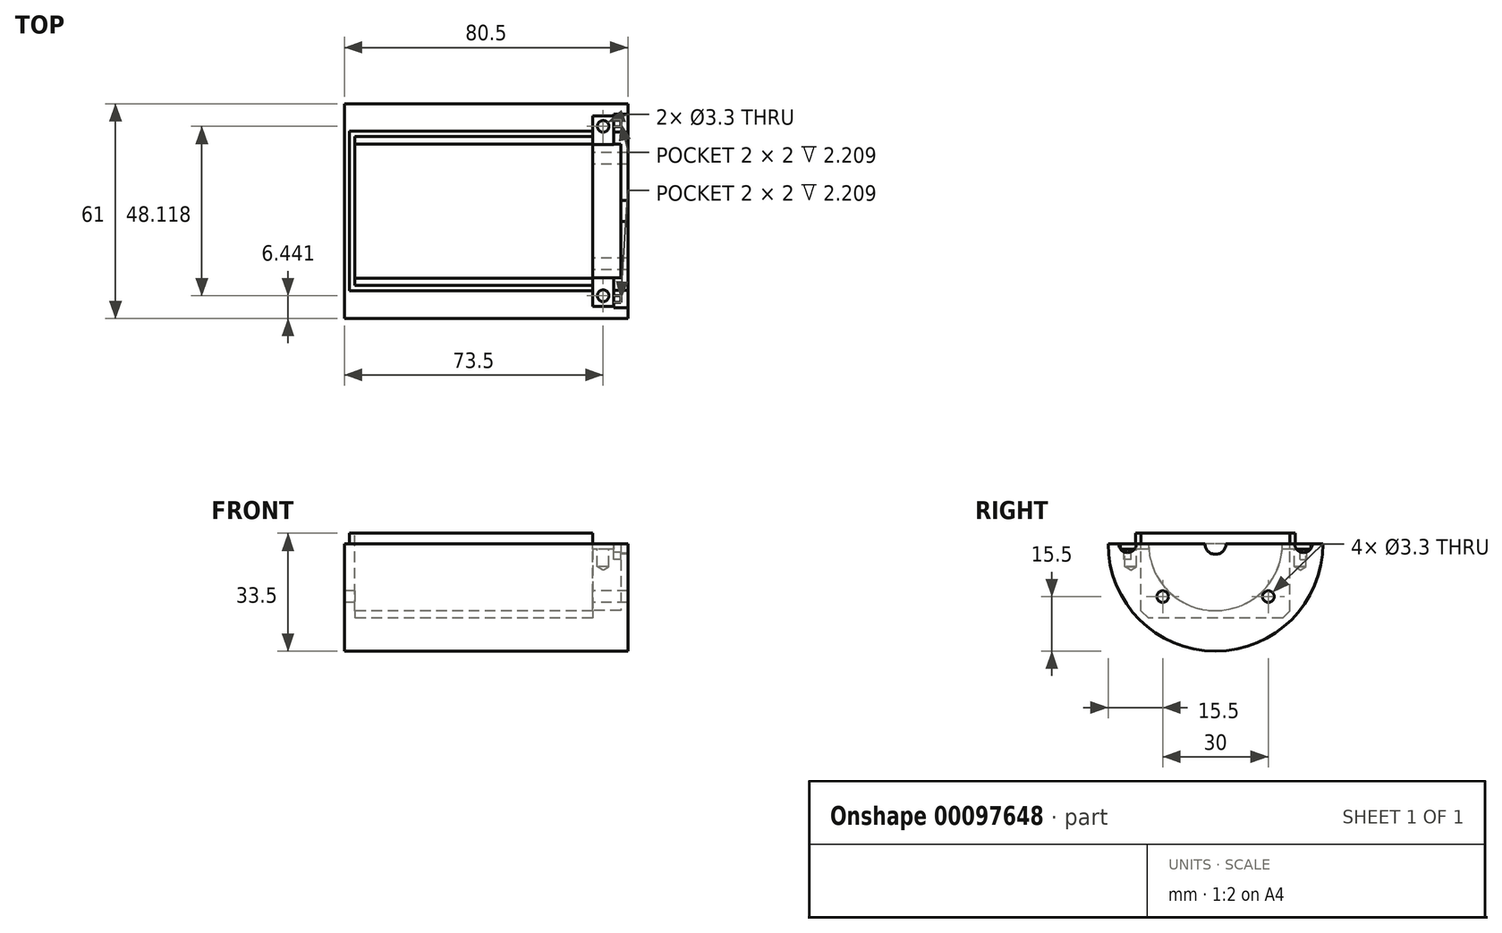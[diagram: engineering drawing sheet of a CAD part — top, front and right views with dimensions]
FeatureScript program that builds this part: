
annotation { "Feature Type Name" : "Feature", "Feature Type Description" : "" }
export const myFeature = defineFeature(function(context is Context, id is Id, definition is map)
    precondition{}
    {
        {
            var Q0;
            Q0=qCreatedBy(makeId("Right.planeOp"),FACE);
            var sketch = newSketch(context, id + "F0", { "sketchPlane" : qUnion([Q0])});
            skArc(sketch, "E0", {"start": v(-30.5, 0) * mm, "mid": v(0, -30.5) * mm, "end": v(30.5, 0) * mm});
            skLineSegment(sketch, "E1.bottom", {"start": v(19.03, -21.15) * mm, "end": v(-19.03, -21.15) * mm});
            skLineSegment(sketch, "E1.left", {"start": v(21.15, -19.03) * mm, "end": v(21.15, 0) * mm});
            skLineSegment(sketch, "E1.right", {"start": v(-21.15, -19.03) * mm, "end": v(-21.15, 0) * mm});
            skLineSegment(sketch, "E2", {"start": v(-30.5, 0) * mm, "end": v(30.5, 0) * mm});
            skPoint(sketch, "E2.endSnap0", {"position": v(21.15, 0) * mm});
            skLineSegment(sketch, "E3", {"start": v(-21.15, -19.03) * mm, "end": v(-19.03, -21.15) * mm});
            skLineSegment(sketch, "E4.MirrorCS", {"start": v(21.15, -19.03) * mm, "end": v(19.03, -21.15) * mm});
            skSolve(sketch);
        }
        {
            var Q0;
            {var subQ0=sQuery(id+"F0.wireOp",EDGE,"E2");var subQ3=sQuery(id+"F0.wireOp",EDGE,"E1.right");var subQ6=makeQuery(id+"F0.imprint","INTERSECT",VERTEX,{"derivedFrom":[subQ3,subQ0]});Q0=makeQuery(id+"F0.imprint","IMPRINT",FACE,{"disambiguationData":[TD([[makeQuery(id+"F0.imprint","IMPRINT",EDGE,{"disambiguationData":[TD([[subQ6,1.0]])],"derivedFrom":subQ3}),1.0]])]});}
            var Q1;
            {var subQ0=sQuery(id+"F0.wireOp",EDGE,"E1.bottom");var subQ5=makeQuery(id+"F0.imprint","INTERSECT",VERTEX,{"derivedFrom":[subQ0,sQuery(id+"F0.wireOp",EDGE,"E3")]});Q1=makeQuery(id+"F0.imprint","IMPRINT",FACE,{"disambiguationData":[TD([[makeQuery(id+"F0.imprint","IMPRINT",EDGE,{"disambiguationData":[TD([[subQ5,1.0]])],"derivedFrom":subQ0}),1.0]])]});}
            var Q2;
            {var subQ0=sQuery(id+"F0.wireOp",EDGE,"E2");var subQ3=sQuery(id+"F0.wireOp",EDGE,"E1.left");var subQ6=makeQuery(id+"F0.imprint","INTERSECT",VERTEX,{"derivedFrom":[subQ3,subQ0]});Q2=makeQuery(id+"F0.imprint","IMPRINT",FACE,{"disambiguationData":[TD([[makeQuery(id+"F0.imprint","IMPRINT",EDGE,{"disambiguationData":[TD([[subQ6,1.0]])],"derivedFrom":subQ3}),-1.0]])]});}
            var Q3;
            {var subQ3=sQuery(id+"F0.wireOp",EDGE,"E4.MirrorCS");Q3=makeQuery(id+"F0.imprint","IMPRINT",FACE,{"disambiguationData":[TD([[makeQuery(id+"F0.imprint","IMPRINT",EDGE,{"derivedFrom":subQ3}),1.0]])]});}
            var Q4;
            {var subQ3=sQuery(id+"F0.wireOp",EDGE,"E3");Q4=makeQuery(id+"F0.imprint","IMPRINT",FACE,{"disambiguationData":[TD([[makeQuery(id+"F0.imprint","IMPRINT",EDGE,{"derivedFrom":subQ3}),-1.0]])]});}
            extrude(context, id + "F1", {"entities" : qUnion([Q0, Q1, Q2, Q3, Q4]), "endBound" : BoundingType.SYMMETRIC, "depth" : 67.5 * mm});
        }
        {
            var Q0;
            Q0=makeQuery(id+"F1.opExtrude","CAP_FACE",FACE,{"disambiguationData":[OSD([sQuery(id+"F0.wireOp",EDGE,"E0"),sQuery(id+"F0.wireOp",EDGE,"E1.bottom"),sQuery(id+"F0.wireOp",EDGE,"E1.left"),sQuery(id+"F0.wireOp",EDGE,"E1.right"),sQuery(id+"F0.wireOp",EDGE,"E2"),sQuery(id+"F0.wireOp",EDGE,"E3"),sQuery(id+"F0.wireOp",EDGE,"E4.MirrorCS")])],"isStart":false});
            var sketch = newSketch(context, id + "F2", { "sketchPlane" : qUnion([Q0])});
            skArc(sketch, "E5", {"start": v(-30.5, 0) * mm, "mid": v(0, -30.5) * mm, "end": v(30.5, 0) * mm});
            skLineSegment(sketch, "E6", {"start": v(-30.5, 0) * mm, "end": v(30.5, 0) * mm});
            skSolve(sketch);
        }
        {
            var Q0;
            Q0=makeQuery(id+"F2.imprint","IMPRINT",FACE,{"disambiguationData":[TD([[makeQuery(id+"F2.imprint","IMPRINT",EDGE,{"derivedFrom":makeQuery(id+"F1.opExtrude","CAP_EDGE",EDGE,{"disambiguationData":[OSD([sQuery(id+"F0.wireOp",EDGE,"E1.bottom")])],"isStart":false})}),-1.0]])]});
            var Q1;
            {var subQ1=sQuery(id+"F2.wireOp",EDGE,"E5");Q1=makeQuery(id+"F2.imprint","IMPRINT",FACE,{"disambiguationData":[TD([[makeQuery(id+"F2.imprint","IMPRINT",EDGE,{"derivedFrom":subQ1}),1.0]])]});}
            extrude(context, id + "F3", {"entities" : qUnion([Q0, Q1]), "operationType" : NewBodyOperationType.ADD, "depth" : 10 * mm});
        }
        {
            var Q0;
            Q0=makeQuery(id+"F1.opExtrude","CAP_FACE",FACE,{"disambiguationData":[OSD([sQuery(id+"F0.wireOp",EDGE,"E0"),sQuery(id+"F0.wireOp",EDGE,"E1.bottom"),sQuery(id+"F0.wireOp",EDGE,"E1.left"),sQuery(id+"F0.wireOp",EDGE,"E1.right"),sQuery(id+"F0.wireOp",EDGE,"E2"),sQuery(id+"F0.wireOp",EDGE,"E3"),sQuery(id+"F0.wireOp",EDGE,"E4.MirrorCS")])],"isStart":true});
            var sketch = newSketch(context, id + "F4", { "sketchPlane" : qUnion([Q0])});
            skArc(sketch, "E7", {"start": v(-30.5, 0) * mm, "mid": v(0, -30.5) * mm, "end": v(30.5, 0) * mm});
            skLineSegment(sketch, "E8", {"start": v(-30.5, 0) * mm, "end": v(30.5, 0) * mm});
            skSolve(sketch);
        }
        {
            var Q0;
            Q0=makeQuery(id+"F4.imprint","IMPRINT",FACE,{"disambiguationData":[TD([[makeQuery(id+"F4.imprint","IMPRINT",EDGE,{"derivedFrom":makeQuery(id+"F1.opExtrude","CAP_EDGE",EDGE,{"disambiguationData":[OSD([sQuery(id+"F0.wireOp",EDGE,"E1.bottom")])],"isStart":true})}),1.0]])]});
            var Q1;
            {var subQ1=sQuery(id+"F4.wireOp",EDGE,"E7");Q1=makeQuery(id+"F4.imprint","IMPRINT",FACE,{"disambiguationData":[TD([[makeQuery(id+"F4.imprint","IMPRINT",EDGE,{"derivedFrom":subQ1}),-1.0]])]});}
            extrude(context, id + "F5", {"entities" : qUnion([Q0, Q1]), "operationType" : NewBodyOperationType.ADD, "depth" : 3 * mm});
        }
        {
            var Q0;
            {var subQ0=sQuery(id+"F0.wireOp",EDGE,"E2");var subQ1=sQuery(id+"F0.wireOp",EDGE,"E0");Q0=makeQuery(id+"F5.boolean.opBoolean","MERGE",FACE,{"derivedFrom":[makeQuery(id+"F3.boolean.opBoolean","MERGE",FACE,{"derivedFrom":[makeQuery(id+"F1.opExtrude","SWEPT_FACE",FACE,{"disambiguationData":[OSD([subQ0]),TDD([makeQuery(id+"F0.imprint","IMPRINT",EDGE,{"disambiguationData":[TD([[makeQuery(id+"F0.imprint","INTERSECT",VERTEX,{"disambiguationData":[OD(0.0)],"derivedFrom":[subQ1,subQ0]}),-1.0]])],"derivedFrom":subQ0})])]}),makeQuery(id+"F1.opExtrude","SWEPT_FACE",FACE,{"disambiguationData":[OSD([subQ0]),TDD([makeQuery(id+"F0.imprint","IMPRINT",EDGE,{"disambiguationData":[TD([[makeQuery(id+"F0.imprint","INTERSECT",VERTEX,{"disambiguationData":[OD(1.0)],"derivedFrom":[subQ1,subQ0]}),1.0]])],"derivedFrom":subQ0})])]}),makeQuery(id+"F3.opExtrude","SWEPT_FACE",FACE,{"disambiguationData":[OSD([sQuery(id+"F2.wireOp",EDGE,"E6")])]})]}),makeQuery(id+"F5.opExtrude","SWEPT_FACE",FACE,{"disambiguationData":[OSD([sQuery(id+"F4.wireOp",EDGE,"E8")])]})]});}
            var sketch = newSketch(context, id + "F6", { "sketchPlane" : qUnion([Q0])});
            skLineSegment(sketch, "E9.bottom", {"start": v(33.75, 0) * mm, "end": v(41.75, 0) * mm});
            skLineSegment(sketch, "E9.top", {"start": v(33.75, 19) * mm, "end": v(41.75, 19) * mm});
            skLineSegment(sketch, "E9.left", {"start": v(33.75, 0) * mm, "end": v(33.75, 19) * mm});
            skLineSegment(sketch, "E9.right", {"start": v(41.75, 0) * mm, "end": v(41.75, 19) * mm});
            skLineSegment(sketch, "E10.bottom", {"start": v(43.75, 0) * mm, "end": v(41.75, 0) * mm});
            skLineSegment(sketch, "E10.top", {"start": v(43.75, 3) * mm, "end": v(41.75, 3) * mm});
            skLineSegment(sketch, "E10.left", {"start": v(43.75, 0) * mm, "end": v(43.75, 3) * mm});
            skLineSegment(sketch, "E10.right", {"start": v(41.75, 0) * mm, "end": v(41.75, 3) * mm});
            skLineSegment(sketch, "E11.bottom", {"start": v(39.75, -22.5) * mm, "end": v(43.75, -22.5) * mm});
            skLineSegment(sketch, "E11.top", {"start": v(39.75, -27.5) * mm, "end": v(43.75, -27.5) * mm});
            skLineSegment(sketch, "E11.left", {"start": v(39.75, -22.5) * mm, "end": v(39.75, -27.5) * mm});
            skLineSegment(sketch, "E11.right", {"start": v(43.75, -22.5) * mm, "end": v(43.75, -27.5) * mm});
            skLineSegment(sketch, "E12.MirrorCS", {"start": v(39.75, 22.5) * mm, "end": v(39.75, 27.5) * mm});
            skLineSegment(sketch, "E13.MirrorCS", {"start": v(39.75, 22.5) * mm, "end": v(43.75, 22.5) * mm});
            skLineSegment(sketch, "E14.MirrorCS", {"start": v(39.75, 27.5) * mm, "end": v(43.75, 27.5) * mm});
            skLineSegment(sketch, "E15.MirrorCS", {"start": v(43.75, 22.5) * mm, "end": v(43.75, 27.5) * mm});
            skLineSegment(sketch, "E16", {"start": v(39.75, -25) * mm, "end": v(43.75, -25) * mm});
            skLineSegment(sketch, "E17.MirrorCS", {"start": v(39.75, 25) * mm, "end": v(43.75, 25) * mm});
            skSolve(sketch);
        }
        {
            var Q0;
            Q0=makeQuery(id+"F6.imprint","IMPRINT",FACE,{"disambiguationData":[TD([[makeQuery(id+"F6.imprint","IMPRINT",EDGE,{"derivedFrom":sQuery(id+"F6.wireOp",EDGE,"E9.bottom")}),1.0]])]});
            var Q1;
            Q1=makeQuery(id+"F6.imprint","IMPRINT",FACE,{"disambiguationData":[TD([[makeQuery(id+"F6.imprint","IMPRINT",EDGE,{"derivedFrom":sQuery(id+"F6.wireOp",EDGE,"E10.bottom")}),-1.0]])]});
            var Q2;
            Q2=sQuery(id+"F6.wireOp",EDGE,"E9.bottom");
            revolve(context, id + "F7", {"operationType" : NewBodyOperationType.REMOVE, "entities" : qUnion([Q0, Q1]), "axis" : qUnion([Q2]), "revolveType" : RevolveType.FULL});
        }
        {
            var Q0;
            {var subQ0=sQuery(id+"F6.wireOp",EDGE,"E11.top");Q0=makeQuery(id+"F6.imprint","IMPRINT",FACE,{"disambiguationData":[TD([[makeQuery(id+"F6.imprint","IMPRINT",EDGE,{"derivedFrom":subQ0}),1.0]])]});}
            var Q1;
            Q1=sQuery(id+"F6.wireOp",EDGE,"E16");
            revolve(context, id + "F8", {"operationType" : NewBodyOperationType.REMOVE, "entities" : qUnion([Q0]), "axis" : qUnion([Q1]), "revolveType" : RevolveType.FULL, "oppositeDirection" : true});
        }
        {
            var Q0;
            {var subQ0=sQuery(id+"F6.wireOp",EDGE,"E13.MirrorCS");Q0=makeQuery(id+"F6.imprint","IMPRINT",FACE,{"disambiguationData":[TD([[makeQuery(id+"F6.imprint","IMPRINT",EDGE,{"derivedFrom":subQ0}),1.0]])]});}
            var Q1;
            Q1=sQuery(id+"F6.wireOp",EDGE,"E17.MirrorCS");
            revolve(context, id + "F9", {"operationType" : NewBodyOperationType.REMOVE, "entities" : qUnion([Q0]), "axis" : qUnion([Q1]), "revolveType" : RevolveType.FULL, "oppositeDirection" : true});
        }
        {
            var Q0;
            {var subQ16=sQuery(id+"F6.wireOp",EDGE,"E9.bottom");Q0=makeQuery(id+"F6.imprint","IMPRINT",FACE,{"disambiguationData":[TD([[makeQuery(id+"F6.imprint","IMPRINT",EDGE,{"derivedFrom":subQ16}),-1.0]])]});}
            var sketch = newSketch(context, id + "F10", { "sketchPlane" : qUnion([Q0])});
            skLineSegment(sketch, "E18.bottom", {"start": v(41.75, -26) * mm, "end": v(39.75, -26) * mm});
            skLineSegment(sketch, "E18.top", {"start": v(41.75, -24) * mm, "end": v(39.75, -24) * mm});
            skLineSegment(sketch, "E18.left", {"start": v(41.75, -26) * mm, "end": v(41.75, -24) * mm});
            skPoint(sketch, "E18.middle", {"position": v(39.75, -25) * mm});
            skLineSegment(sketch, "E19", {"start": v(39.75, -24) * mm, "end": v(39.75, -26) * mm});
            skPoint(sketch, "E18.right.end.orphan", {"position": v(37.75, -24) * mm});
            skPoint(sketch, "E20.orphan", {"position": v(37.75, -26) * mm});
            skLineSegment(sketch, "E21.MirrorCS", {"start": v(41.75, 24) * mm, "end": v(39.75, 24) * mm});
            skLineSegment(sketch, "E22.MirrorCS", {"start": v(41.75, 26) * mm, "end": v(41.75, 24) * mm});
            skLineSegment(sketch, "E23.MirrorCS", {"start": v(41.75, 26) * mm, "end": v(39.75, 26) * mm});
            skLineSegment(sketch, "E24.MirrorCS", {"start": v(39.75, 24) * mm, "end": v(39.75, 26) * mm});
            skSolve(sketch);
        }
        {
            var Q0;
            {var subQ5=sQuery(id+"F10.wireOp",EDGE,"E18.bottom");Q0=makeQuery(id+"F10.imprint","IMPRINT",FACE,{"disambiguationData":[TD([[makeQuery(id+"F10.imprint","IMPRINT",EDGE,{"derivedFrom":subQ5}),-1.0]])]});}
            var Q1;
            {var subQ2=sQuery(id+"F10.wireOp",EDGE,"E21.MirrorCS");Q1=makeQuery(id+"F10.imprint","IMPRINT",FACE,{"disambiguationData":[TD([[makeQuery(id+"F10.imprint","IMPRINT",EDGE,{"derivedFrom":subQ2}),-1.0]])]});}
            extrude(context, id + "F11", {"entities" : qUnion([Q0, Q1]), "operationType" : NewBodyOperationType.REMOVE, "oppositeDirection" : true, "depth" : 4.5 * mm});
        }
        {
            var Q0;
            {var subQ0=sQuery(id+"F0.wireOp",EDGE,"E2");var subQ1=sQuery(id+"F0.wireOp",EDGE,"E0");Q0=makeQuery(id+"F5.boolean.opBoolean","MERGE",FACE,{"derivedFrom":[makeQuery(id+"F3.boolean.opBoolean","MERGE",FACE,{"derivedFrom":[makeQuery(id+"F1.opExtrude","SWEPT_FACE",FACE,{"disambiguationData":[OSD([subQ0]),TDD([makeQuery(id+"F0.imprint","IMPRINT",EDGE,{"disambiguationData":[TD([[makeQuery(id+"F0.imprint","INTERSECT",VERTEX,{"disambiguationData":[OD(0.0)],"derivedFrom":[subQ1,subQ0]}),-1.0]])],"derivedFrom":subQ0})])]}),makeQuery(id+"F1.opExtrude","SWEPT_FACE",FACE,{"disambiguationData":[OSD([subQ0]),TDD([makeQuery(id+"F0.imprint","IMPRINT",EDGE,{"disambiguationData":[TD([[makeQuery(id+"F0.imprint","INTERSECT",VERTEX,{"disambiguationData":[OD(1.0)],"derivedFrom":[subQ1,subQ0]}),1.0]])],"derivedFrom":subQ0})])]}),makeQuery(id+"F3.opExtrude","SWEPT_FACE",FACE,{"disambiguationData":[OSD([sQuery(id+"F2.wireOp",EDGE,"E6")])]})]}),makeQuery(id+"F5.opExtrude","SWEPT_FACE",FACE,{"disambiguationData":[OSD([sQuery(id+"F4.wireOp",EDGE,"E8")])]})]});}
            var sketch = newSketch(context, id + "F12", { "sketchPlane" : qUnion([Q0])});
            skLineSegment(sketch, "E25.bottom", {"start": v(33.75, 27.06) * mm, "end": v(39.75, 27.06) * mm});
            skLineSegment(sketch, "E25.top", {"start": v(33.75, -27.06) * mm, "end": v(39.75, -27.06) * mm});
            skLineSegment(sketch, "E25.left", {"start": v(33.75, 27.06) * mm, "end": v(33.75, -27.06) * mm});
            skLineSegment(sketch, "E25.right", {"start": v(39.75, 27.06) * mm, "end": v(39.75, -27.06) * mm});
            skPoint(sketch, "E26", {"position": v(36.75, 24.06) * mm});
            skPoint(sketch, "E27.MirrorP", {"position": v(36.75, -24.06) * mm});
            skSolve(sketch);
        }
        {
            var Q0;
            {var subQ7=sQuery(id+"F12.wireOp",EDGE,"E25.bottom");Q0=makeQuery(id+"F12.imprint","IMPRINT",FACE,{"disambiguationData":[TD([[makeQuery(id+"F12.imprint","IMPRINT",EDGE,{"derivedFrom":subQ7}),-1.0]])]});}
            var Q1;
            {var subQ4=sQuery(id+"F12.wireOp",EDGE,"E25.top");Q1=makeQuery(id+"F12.imprint","IMPRINT",FACE,{"disambiguationData":[TD([[makeQuery(id+"F12.imprint","IMPRINT",EDGE,{"derivedFrom":subQ4}),1.0]])]});}
            var Q2;
            {var subQ0=sQuery(id+"F12.wireOp",EDGE,"E25.left");var subQ1=makeQuery(id+"F7.opRevolve","SWEPT_FACE",FACE,{"disambiguationData":[OSD([sQuery(id+"F6.wireOp",EDGE,"E9.top")])]});var subQ2=sQuery(id+"F0.wireOp",EDGE,"E2");var subQ3=sQuery(id+"F0.wireOp",EDGE,"E0");var subQ4=makeQuery(id+"F5.boolean.opBoolean","MERGE",FACE,{"derivedFrom":[makeQuery(id+"F3.boolean.opBoolean","MERGE",FACE,{"derivedFrom":[makeQuery(id+"F1.opExtrude","SWEPT_FACE",FACE,{"disambiguationData":[OSD([subQ2]),TDD([makeQuery(id+"F0.imprint","IMPRINT",EDGE,{"disambiguationData":[TD([[makeQuery(id+"F0.imprint","INTERSECT",VERTEX,{"disambiguationData":[OD(0.0)],"derivedFrom":[subQ3,subQ2]}),-1.0]])],"derivedFrom":subQ2})])]}),makeQuery(id+"F1.opExtrude","SWEPT_FACE",FACE,{"disambiguationData":[OSD([subQ2]),TDD([makeQuery(id+"F0.imprint","IMPRINT",EDGE,{"disambiguationData":[TD([[makeQuery(id+"F0.imprint","INTERSECT",VERTEX,{"disambiguationData":[OD(1.0)],"derivedFrom":[subQ3,subQ2]}),1.0]])],"derivedFrom":subQ2})])]}),makeQuery(id+"F3.opExtrude","SWEPT_FACE",FACE,{"disambiguationData":[OSD([sQuery(id+"F2.wireOp",EDGE,"E6")])]})]}),makeQuery(id+"F5.opExtrude","SWEPT_FACE",FACE,{"disambiguationData":[OSD([sQuery(id+"F4.wireOp",EDGE,"E8")])]})]});var subQ5=makeQuery(id+"F7.boolean.opBoolean","INTERSECT",EDGE,{"disambiguationData":[OD(0.0)],"derivedFrom":[subQ4,subQ1]});var subQ6=makeQuery(id+"F12.imprint","INTERSECT",VERTEX,{"derivedFrom":[subQ5,subQ0]});var subQ7=makeQuery(id+"F7.boolean.opBoolean","INTERSECT",EDGE,{"disambiguationData":[OD(1.0)],"derivedFrom":[subQ4,subQ1]});var subQ8=makeQuery(id+"F12.imprint","INTERSECT",VERTEX,{"derivedFrom":[subQ7,subQ0]});Q2=makeQuery(id+"F12.imprint","IMPRINT",FACE,{"disambiguationData":[TD([[makeQuery(id+"F12.imprint","IMPRINT",EDGE,{"disambiguationData":[TD([[subQ6,-1.0],[subQ8,1.0]])],"derivedFrom":subQ0}),1.0]])]});}
            extrude(context, id + "F13", {"entities" : qUnion([Q0, Q1, Q2]), "operationType" : NewBodyOperationType.REMOVE, "oppositeDirection" : true, "depth" : 1.5 * mm});
        }
        {
            var Q0;
            Q0=sQuery(id+"F12.wireOp",VERTEX,"E26");
            var Q1;
            Q1=sQuery(id+"F12.wireOp",VERTEX,"E27.MirrorP");
            var Q2;
            Q2=makeQuery(id+"F1.opExtrude","SWEPT_BODY",BODY,{"disambiguationData":[OSD([sQuery(id+"F0.wireOp",EDGE,"E0"),sQuery(id+"F0.wireOp",EDGE,"E1.bottom"),sQuery(id+"F0.wireOp",EDGE,"E1.left"),sQuery(id+"F0.wireOp",EDGE,"E1.right"),sQuery(id+"F0.wireOp",EDGE,"E2"),sQuery(id+"F0.wireOp",EDGE,"E3"),sQuery(id+"F0.wireOp",EDGE,"E4.MirrorCS")])]});
            hole(context, id + "F14", {"style" : HoleStyle.SIMPLE, "endStyle" : HoleEndStyle.BLIND, "standardTappedOrClearance" : lookupTablePath({ "standard" : "ISO", "fit" : "Normal", "size" : "M3", "type" : "Clearance" }), "standardBlindInLast" : lookupTablePath({ "fit" : "Standard", "standard" : "ISO", "size" : "M3", "type" : "Clearance" }), "holeDiameter" : 3.3 * mm, "holeDepth" : 5 * mm, "locations" : qUnion([Q0, Q1]), "scope" : qUnion([Q2])});
        }
        {
            var Q0;
            {var subQ0=sQuery(id+"F4.wireOp",EDGE,"E8");var subQ1=sQuery(id+"F4.wireOp",EDGE,"E7");var subQ2=sQuery(id+"F2.wireOp",EDGE,"E6");var subQ3=sQuery(id+"F2.wireOp",EDGE,"E5");var subQ4=sQuery(id+"F0.wireOp",EDGE,"E0");var subQ5=sQuery(id+"F0.wireOp",EDGE,"E1.left");var subQ6=sQuery(id+"F0.wireOp",EDGE,"E1.right");var subQ7=sQuery(id+"F0.wireOp",EDGE,"E2");Q0=makeQuery(id+"F13.boolean.opBoolean","SPLIT",FACE,{"disambiguationData":[TD([makeQuery(id+"F1.opExtrude","SWEPT_FACE",FACE,{"disambiguationData":[OSD([subQ4])]}),makeQuery(id+"F1.opExtrude","SWEPT_FACE",FACE,{"disambiguationData":[OSD([subQ5])]}),makeQuery(id+"F1.opExtrude","SWEPT_FACE",FACE,{"disambiguationData":[OSD([subQ6])]}),makeQuery(id+"F3.opExtrude","SWEPT_FACE",FACE,{"disambiguationData":[OSD([subQ3])]}),makeQuery(id+"F3.opExtrude","CAP_FACE",FACE,{"disambiguationData":[OSD([subQ3,subQ2])],"isStart":false}),makeQuery(id+"F5.opExtrude","SWEPT_FACE",FACE,{"disambiguationData":[OSD([subQ1])]}),makeQuery(id+"F5.opExtrude","CAP_FACE",FACE,{"disambiguationData":[OSD([subQ1,subQ0])],"isStart":true}),makeQuery(id+"F5.opExtrude","CAP_FACE",FACE,{"disambiguationData":[OSD([subQ1,subQ0])],"isStart":false}),makeQuery(id+"F8.boolean.opBoolean","COPY",FACE,{"derivedFrom":makeQuery(id+"F8.opRevolve","SWEPT_FACE",FACE,{"disambiguationData":[OSD([sQuery(id+"F6.wireOp",EDGE,"E11.top")])]})}),makeQuery(id+"F8.boolean.opBoolean","COPY",FACE,{"derivedFrom":makeQuery(id+"F8.opRevolve","SWEPT_FACE",FACE,{"disambiguationData":[OSD([sQuery(id+"F6.wireOp",EDGE,"E11.left")])]})}),makeQuery(id+"F9.boolean.opBoolean","COPY",FACE,{"derivedFrom":makeQuery(id+"F9.opRevolve","SWEPT_FACE",FACE,{"disambiguationData":[OSD([sQuery(id+"F6.wireOp",EDGE,"E12.MirrorCS")])]})}),makeQuery(id+"F9.boolean.opBoolean","COPY",FACE,{"derivedFrom":makeQuery(id+"F9.opRevolve","SWEPT_FACE",FACE,{"disambiguationData":[OSD([sQuery(id+"F6.wireOp",EDGE,"E13.MirrorCS")])]})}),makeQuery(id+"F11.opExtrude","SWEPT_FACE",FACE,{"disambiguationData":[OSD([sQuery(id+"F10.wireOp",EDGE,"E19")])]}),makeQuery(id+"F11.opExtrude","SWEPT_FACE",FACE,{"disambiguationData":[OSD([sQuery(id+"F10.wireOp",EDGE,"E24.MirrorCS")])]}),makeQuery(id+"F13.opExtrude","SWEPT_FACE",FACE,{"disambiguationData":[OSD([sQuery(id+"F12.wireOp",EDGE,"E25.bottom")])]}),makeQuery(id+"F13.opExtrude","SWEPT_FACE",FACE,{"disambiguationData":[OSD([sQuery(id+"F12.wireOp",EDGE,"E25.top")])]}),makeQuery(id+"F13.opExtrude","SWEPT_FACE",FACE,{"disambiguationData":[OSD([sQuery(id+"F12.wireOp",EDGE,"E25.left")])]})])],"derivedFrom":makeQuery(id+"F5.boolean.opBoolean","MERGE",FACE,{"derivedFrom":[makeQuery(id+"F3.boolean.opBoolean","MERGE",FACE,{"derivedFrom":[makeQuery(id+"F1.opExtrude","SWEPT_FACE",FACE,{"disambiguationData":[OSD([subQ7]),TDD([makeQuery(id+"F0.imprint","IMPRINT",EDGE,{"disambiguationData":[TD([[makeQuery(id+"F0.imprint","INTERSECT",VERTEX,{"disambiguationData":[OD(0.0)],"derivedFrom":[subQ4,subQ7]}),-1.0]])],"derivedFrom":subQ7})])]}),makeQuery(id+"F1.opExtrude","SWEPT_FACE",FACE,{"disambiguationData":[OSD([subQ7]),TDD([makeQuery(id+"F0.imprint","IMPRINT",EDGE,{"disambiguationData":[TD([[makeQuery(id+"F0.imprint","INTERSECT",VERTEX,{"disambiguationData":[OD(1.0)],"derivedFrom":[subQ4,subQ7]}),1.0]])],"derivedFrom":subQ7})])]}),makeQuery(id+"F3.opExtrude","SWEPT_FACE",FACE,{"disambiguationData":[OSD([subQ2])]})]}),makeQuery(id+"F5.opExtrude","SWEPT_FACE",FACE,{"disambiguationData":[OSD([subQ0])]})]})});}
            var sketch = newSketch(context, id + "F15", { "sketchPlane" : qUnion([Q0])});
            skLineSegment(sketch, "E28.bottom", {"start": v(33.75, 21.15) * mm, "end": v(-33.75, 21.15) * mm});
            skLineSegment(sketch, "E28.top", {"start": v(33.75, 22.65) * mm, "end": v(-33.75, 22.65) * mm});
            skLineSegment(sketch, "E28.left", {"start": v(33.75, 21.15) * mm, "end": v(33.75, 22.65) * mm});
            skLineSegment(sketch, "E28.right", {"start": v(-33.75, 21.15) * mm, "end": v(-33.75, 22.65) * mm});
            skPoint(sketch, "E29.oppositeSnap0", {"position": v(-36.75, 0) * mm});
            skLineSegment(sketch, "E29.bottom", {"start": v(-33.75, 22.65) * mm, "end": v(-35.25, 22.65) * mm});
            skLineSegment(sketch, "E29.top", {"start": v(-33.75, 0) * mm, "end": v(-35.25, 0) * mm});
            skLineSegment(sketch, "E29.left", {"start": v(-33.75, 22.65) * mm, "end": v(-33.75, 0) * mm});
            skLineSegment(sketch, "E29.right", {"start": v(-35.25, 22.65) * mm, "end": v(-35.25, 0) * mm});
            skLineSegment(sketch, "E30.MirrorCS", {"start": v(33.75, -21.15) * mm, "end": v(-33.75, -21.15) * mm});
            skLineSegment(sketch, "E31.MirrorCS", {"start": v(33.75, -22.65) * mm, "end": v(-33.75, -22.65) * mm});
            skLineSegment(sketch, "E32.MirrorCS", {"start": v(33.75, -21.15) * mm, "end": v(33.75, -22.65) * mm});
            skLineSegment(sketch, "E33.MirrorCS", {"start": v(-33.75, -22.65) * mm, "end": v(-35.25, -22.65) * mm});
            skLineSegment(sketch, "E34.MirrorCS", {"start": v(-35.25, -22.65) * mm, "end": v(-35.25, 0) * mm});
            skLineSegment(sketch, "E35.MirrorCS", {"start": v(-33.75, -22.65) * mm, "end": v(-33.75, 0) * mm});
            skSolve(sketch);
        }
        {
            var Q0;
            {var subQ0=sQuery(id+"F15.wireOp",EDGE,"E28.bottom");Q0=makeQuery(id+"F15.imprint","IMPRINT",FACE,{"disambiguationData":[TD([[makeQuery(id+"F15.imprint","IMPRINT",EDGE,{"derivedFrom":subQ0}),-1.0]])]});}
            var Q1;
            {var subQ3=sQuery(id+"F15.wireOp",EDGE,"E29.bottom");Q1=makeQuery(id+"F15.imprint","IMPRINT",FACE,{"disambiguationData":[TD([[makeQuery(id+"F15.imprint","IMPRINT",EDGE,{"derivedFrom":subQ3}),1.0]])]});}
            var Q2;
            {var subQ3=sQuery(id+"F15.wireOp",EDGE,"E29.top");Q2=makeQuery(id+"F15.imprint","IMPRINT",FACE,{"disambiguationData":[TD([[makeQuery(id+"F15.imprint","IMPRINT",EDGE,{"derivedFrom":subQ3}),1.0]])]});}
            var Q3;
            {var subQ0=sQuery(id+"F15.wireOp",EDGE,"E30.MirrorCS");Q3=makeQuery(id+"F15.imprint","IMPRINT",FACE,{"disambiguationData":[TD([[makeQuery(id+"F15.imprint","IMPRINT",EDGE,{"derivedFrom":subQ0}),1.0]])]});}
            extrude(context, id + "F16", {"entities" : qUnion([Q0, Q1, Q2, Q3]), "operationType" : NewBodyOperationType.ADD, "depth" : 3 * mm});
        }
        {
            var Q0;
            Q0=makeQuery(id+"F5.opExtrude","CAP_FACE",FACE,{"disambiguationData":[OSD([sQuery(id+"F4.wireOp",EDGE,"E7"),sQuery(id+"F4.wireOp",EDGE,"E8")])],"isStart":false});
            var sketch = newSketch(context, id + "F17", { "sketchPlane" : qUnion([Q0])});
            skPoint(sketch, "E36", {"position": v(-15, -15) * mm});
            skPoint(sketch, "E37.MirrorP", {"position": v(15, -15) * mm});
            skSolve(sketch);
        }
        {
            var Q0;
            Q0=sQuery(id+"F17.wireOp",VERTEX,"E36");
            var Q1;
            Q1=sQuery(id+"F17.wireOp",VERTEX,"E37.MirrorP");
            var Q2;
            Q2=makeQuery(id+"F1.opExtrude","SWEPT_BODY",BODY,{"disambiguationData":[OSD([sQuery(id+"F0.wireOp",EDGE,"E0"),sQuery(id+"F0.wireOp",EDGE,"E1.bottom"),sQuery(id+"F0.wireOp",EDGE,"E1.left"),sQuery(id+"F0.wireOp",EDGE,"E1.right"),sQuery(id+"F0.wireOp",EDGE,"E2"),sQuery(id+"F0.wireOp",EDGE,"E3"),sQuery(id+"F0.wireOp",EDGE,"E4.MirrorCS")])]});
            hole(context, id + "F18", {"style" : HoleStyle.SIMPLE, "endStyle" : HoleEndStyle.THROUGH, "standardTappedOrClearance" : lookupTablePath({ "standard" : "ISO", "fit" : "Normal", "size" : "M3", "type" : "Clearance" }), "standardBlindInLast" : lookupTablePath({ "fit" : "Standard", "standard" : "ISO", "size" : "M3", "type" : "Clearance" }), "holeDiameter" : 3.3 * mm, "locations" : qUnion([Q0, Q1]), "scope" : qUnion([Q2]), "isTappedThrough" : true});
        }
    });
